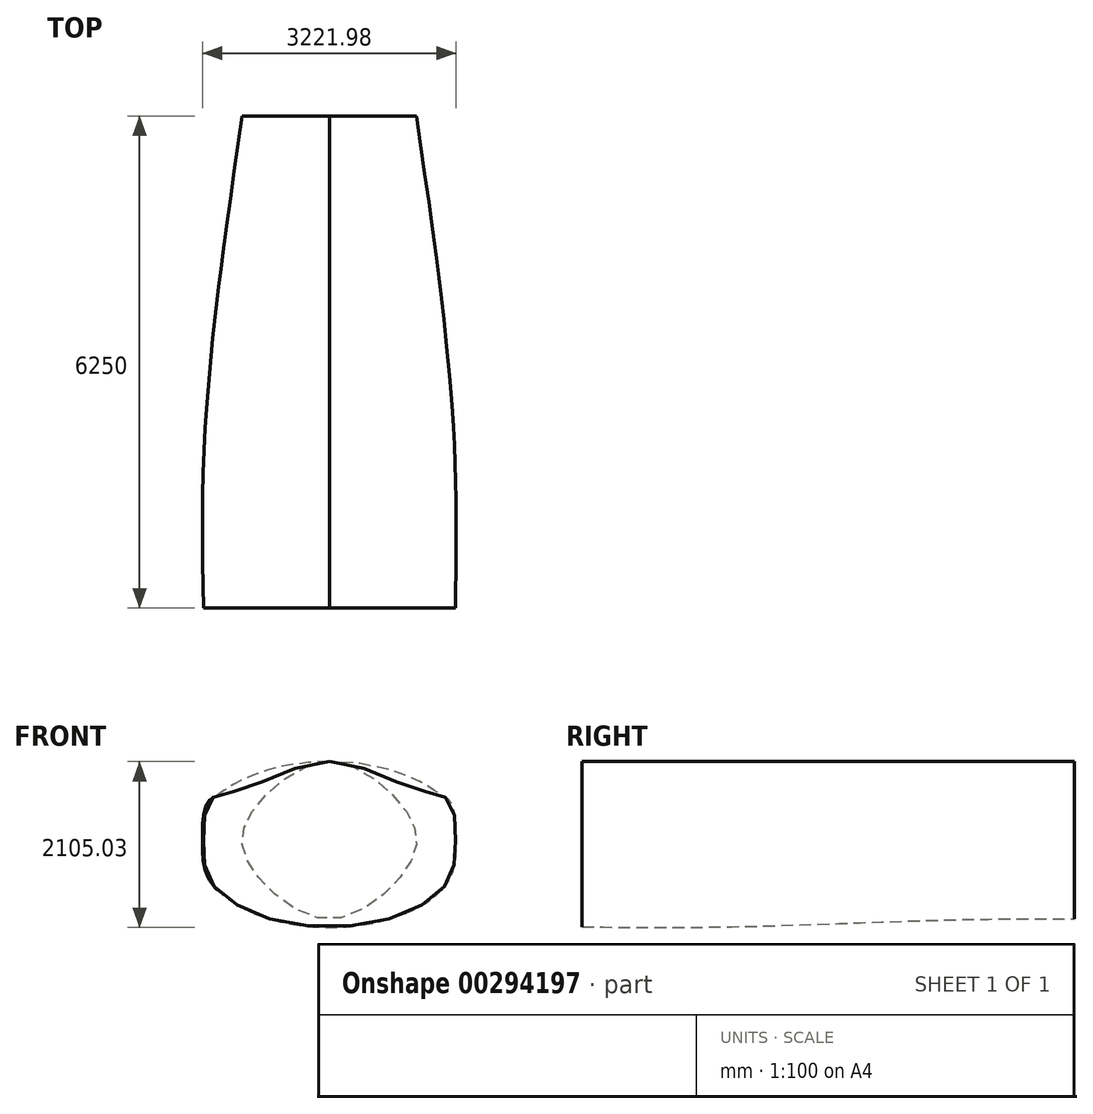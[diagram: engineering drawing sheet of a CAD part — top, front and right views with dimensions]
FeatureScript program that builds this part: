
annotation { "Feature Type Name" : "Feature", "Feature Type Description" : "" }
export const myFeature = defineFeature(function(context is Context, id is Id, definition is map)
    precondition{}
    {
        {
            var Q0;
            Q0=qCreatedBy(makeId("Front.planeOp"),FACE);
            cPlane(context, id + "F0", {"entities" : qUnion([Q0]), "cplaneType" : CPlaneType.OFFSET, "offset" : 1750 * mm, "width" : 150 * mm, "height" : 150 * mm});
        }
        {
            var Q0;
            Q0=qCreatedBy(id+"F0.planeOp",FACE);
            var sketch = newSketch(context, id + "F1", { "sketchPlane" : qUnion([Q0])});
            skPoint(sketch, "E0.middle", {"position": v(0, 0) * mm});
            skFitSpline(sketch, "E1", {"points": [v(0, 1000) * mm, v(1060, 662.5) * mm, v(1517.6, 506.84) * mm, v(1600, 0) * mm, v(1517.6, -506.84) * mm, v(750, -1000) * mm, v(-750, -1000) * mm, v(-1517.6, -506.84) * mm, v(-1600, 0) * mm, v(-1517.6, 506.84) * mm, v(-1060, 662.5) * mm, v(0, 1000) * mm]});
            skSolve(sketch);
        }
        {
            var Q0;
            Q0=qCreatedBy(makeId("Front.planeOp"),FACE);
            var sketch = newSketch(context, id + "F2", { "sketchPlane" : qUnion([Q0])});
            skPoint(sketch, "E2.middle", {"position": v(0, 0) * mm});
            skFitSpline(sketch, "E3", {"points": [v(0, 1000) * mm, v(1060, 662.5) * mm, v(1517.6, 506.84) * mm, v(1600, 0) * mm, v(1517.6, -506.84) * mm, v(750, -1000) * mm, v(-750, -1000) * mm, v(-1517.6, -506.84) * mm, v(-1600, 0) * mm, v(-1517.6, 506.84) * mm, v(-1060, 662.5) * mm, v(0, 1000) * mm]});
            skSolve(sketch);
        }
        {
            var Q0;
            Q0=qCreatedBy(makeId("Front.planeOp"),FACE);
            cPlane(context, id + "F3", {"entities" : qUnion([Q0]), "cplaneType" : CPlaneType.OFFSET, "offset" : 3500 * mm, "oppositeDirection" : true, "width" : 150 * mm, "height" : 150 * mm});
        }
        {
            var Q0;
            Q0=qCreatedBy(id+"F3.planeOp",FACE);
            var sketch = newSketch(context, id + "F4", { "sketchPlane" : qUnion([Q0])});
            skPoint(sketch, "E4.middle", {"position": v(0, 0) * mm});
            skFitSpline(sketch, "E5", {"points": [v(0, 1000) * mm, v(1060, 662.5) * mm, v(1250, 0) * mm, v(1060, -662.5) * mm, v(0, -1000) * mm, v(-1060, -662.5) * mm, v(-1250, 0) * mm, v(-1060, 662.5) * mm, v(0, 1000) * mm]});
            skSolve(sketch);
        }
        {
            var Q0;
            Q0=qCreatedBy(makeId("Front.planeOp"),FACE);
            cPlane(context, id + "F5", {"entities" : qUnion([Q0]), "cplaneType" : CPlaneType.OFFSET, "offset" : 4500 * mm, "oppositeDirection" : true, "width" : 150 * mm, "height" : 150 * mm});
        }
        {
            var Q0;
            Q0=qCreatedBy(id+"F5.planeOp",FACE);
            var sketch = newSketch(context, id + "F6", { "sketchPlane" : qUnion([Q0])});
            skPoint(sketch, "E6.middle", {"position": v(0, 0) * mm});
            skFitSpline(sketch, "E7", {"points": [v(0, 1000) * mm, v(848, 530) * mm, v(1108.5, 0) * mm, v(848, -530) * mm, v(0, -1000) * mm, v(-848, -530) * mm, v(-1108.5, 0) * mm, v(-848, 530) * mm, v(0, 1000) * mm]});
            skSolve(sketch);
        }
        {
            var Q0;
            Q0=makeQuery(id+"F1.imprint","IMPRINT",FACE,{"disambiguationData":[TD([[makeQuery(id+"F1.imprint","IMPRINT",EDGE,{"derivedFrom":sQuery(id+"F1.wireOp",EDGE,"E1")}),-1.0]])]});
            var Q1;
            Q1=makeQuery(id+"F2.imprint","IMPRINT",FACE,{"disambiguationData":[TD([[makeQuery(id+"F2.imprint","IMPRINT",EDGE,{"derivedFrom":sQuery(id+"F2.wireOp",EDGE,"E3")}),-1.0]])]});
            var Q2;
            Q2=makeQuery(id+"F4.imprint","IMPRINT",FACE,{"disambiguationData":[TD([[makeQuery(id+"F4.imprint","IMPRINT",EDGE,{"derivedFrom":sQuery(id+"F4.wireOp",EDGE,"E5")}),-1.0]])]});
            var Q3;
            Q3=makeQuery(id+"F6.imprint","IMPRINT",FACE,{"disambiguationData":[TD([[makeQuery(id+"F6.imprint","IMPRINT",EDGE,{"derivedFrom":sQuery(id+"F6.wireOp",EDGE,"E7")}),-1.0]])]});
            loft(context, id + "F7", {"sheetProfilesArray" : [{ "sheetProfileEntities" : qUnion([Q0]) }, { "sheetProfileEntities" : qUnion([Q1]) }, { "sheetProfileEntities" : qUnion([Q2]) }, { "sheetProfileEntities" : qUnion([Q3]) }]});
        }
    });
